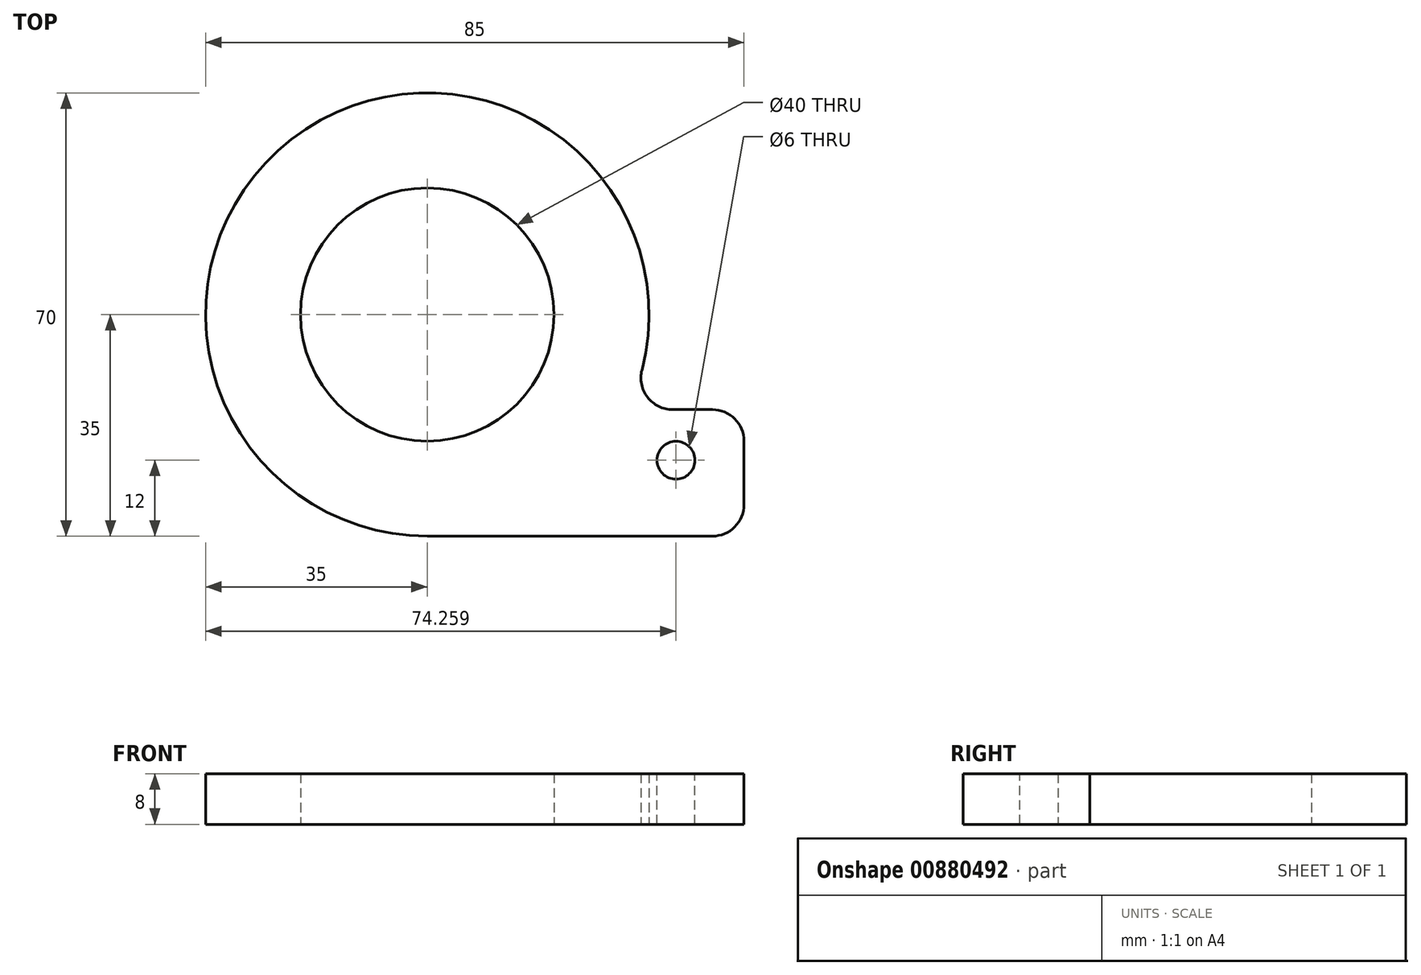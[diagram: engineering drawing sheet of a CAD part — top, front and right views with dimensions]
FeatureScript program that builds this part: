
annotation { "Feature Type Name" : "Feature", "Feature Type Description" : "" }
export const myFeature = defineFeature(function(context is Context, id is Id, definition is map)
    precondition{}
    {
        {
            var Q0;
            Q0=qCreatedBy(makeId("Top.planeOp"),FACE);
            var sketch = newSketch(context, id + "F0", { "sketchPlane" : qUnion([Q0])});
            skCircle(sketch, "E0", {"center": v(0, 0) * mm, "radius": 20 * mm});
            skArc(sketch, "E1", {"start": v(31.62, -15) * mm, "mid": v(-18.7, 29.58) * mm, "end": v(0, -35) * mm});
            skLineSegment(sketch, "E2", {"start": v(0, -35) * mm, "end": v(50, -35) * mm});
            skLineSegment(sketch, "E3", {"start": v(50, -35) * mm, "end": v(50, -15) * mm});
            skLineSegment(sketch, "E4", {"start": v(50, -15) * mm, "end": v(31.62, -15) * mm});
            skSolve(sketch);
        }
        {
            var Q0;
            Q0=makeQuery(id+"F0.imprint","IMPRINT",FACE,{"disambiguationData":[TD([[makeQuery(id+"F0.imprint","IMPRINT",EDGE,{"derivedFrom":sQuery(id+"F0.wireOp",EDGE,"E0")}),-1.0]])]});
            extrude(context, id + "F1", {"entities" : qUnion([Q0]), "depth" : 8 * mm, "offsetDistance" : 25 * mm});
        }
        {
            var Q0;
            Q0=makeQuery(id+"F1.opExtrude","SWEPT_EDGE",EDGE,{"disambiguationData":[OSD([sQuery(id+"F0.wireOp",EDGE,"E1"),sQuery(id+"F0.wireOp",EDGE,"E4")])]});
            var Q1;
            Q1=makeQuery(id+"F1.opExtrude","SWEPT_EDGE",EDGE,{"disambiguationData":[OSD([sQuery(id+"F0.wireOp",EDGE,"E3"),sQuery(id+"F0.wireOp",EDGE,"E4")])]});
            var Q2;
            Q2=makeQuery(id+"F1.opExtrude","SWEPT_EDGE",EDGE,{"disambiguationData":[OSD([sQuery(id+"F0.wireOp",EDGE,"E2"),sQuery(id+"F0.wireOp",EDGE,"E3")])]});
            fillet(context, id + "F2", {"entities" : qUnion([Q0, Q1, Q2]), "radius" : 5 * mm, "tangentPropagation" : true, "allowEdgeOverflow" : false});
        }
        {
            var Q0;
            Q0=makeQuery(id+"F1.opExtrude","CAP_FACE",FACE,{"disambiguationData":[OSD([sQuery(id+"F0.wireOp",EDGE,"E0"),sQuery(id+"F0.wireOp",EDGE,"E1"),sQuery(id+"F0.wireOp",EDGE,"E2"),sQuery(id+"F0.wireOp",EDGE,"E3"),sQuery(id+"F0.wireOp",EDGE,"E4")])],"isStart":false});
            var sketch = newSketch(context, id + "F3", { "sketchPlane" : qUnion([Q0])});
            skLineSegment(sketch, "E5", {"start": v(0, -20) * mm, "end": v(0, -23) * mm, "construction": true});
            skLineSegment(sketch, "E6", {"start": v(0, -23) * mm, "end": v(46.8, -23) * mm, "construction": true});
            skCircle(sketch, "E7", {"center": v(39.26, -23) * mm, "radius": 3 * mm});
            skSolve(sketch);
        }
        {
            var Q0;
            Q0=makeQuery(id+"F3.imprint","IMPRINT",FACE,{"disambiguationData":[TD([[makeQuery(id+"F3.imprint","IMPRINT",EDGE,{"derivedFrom":sQuery(id+"F3.wireOp",EDGE,"E7")}),1.0]])]});
            extrude(context, id + "F4", {"entities" : qUnion([Q0]), "operationType" : NewBodyOperationType.REMOVE, "endBound" : BoundingType.UP_TO_NEXT, "oppositeDirection" : true, "depth" : 25 * mm, "offsetDistance" : 25 * mm});
        }
    });
